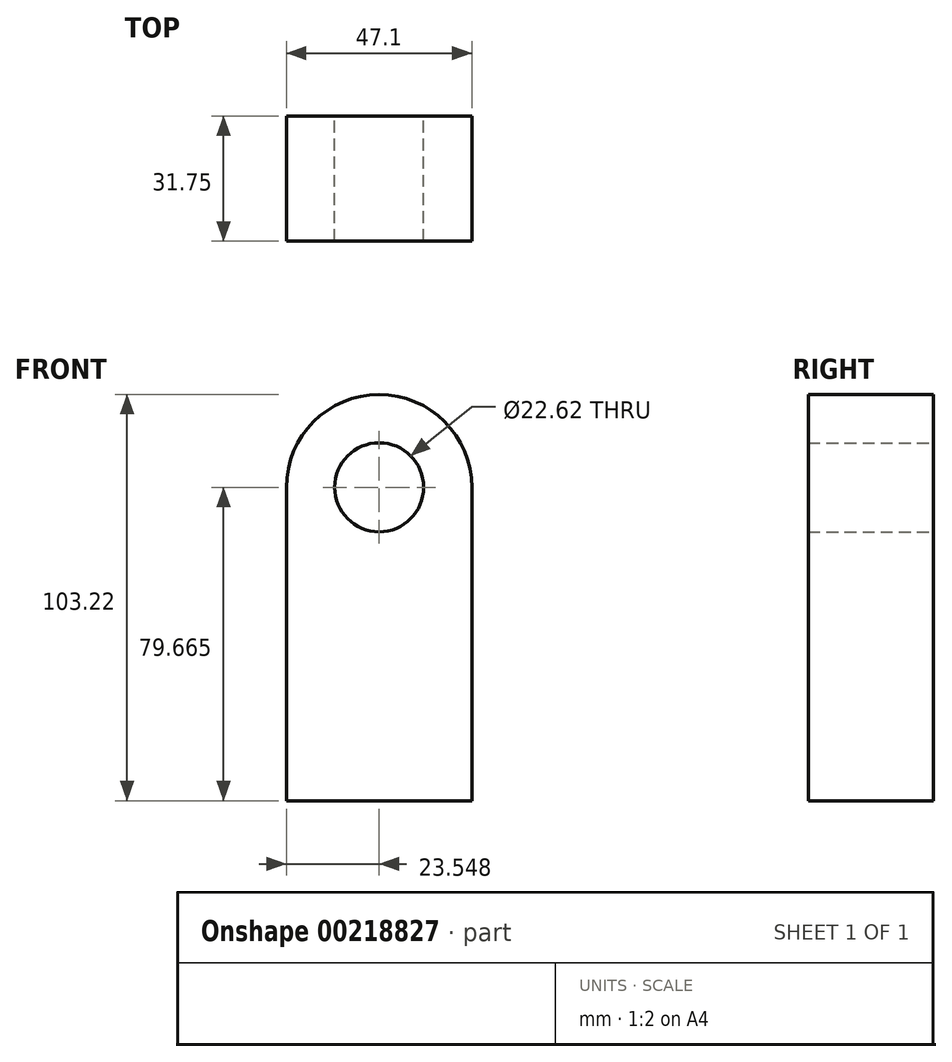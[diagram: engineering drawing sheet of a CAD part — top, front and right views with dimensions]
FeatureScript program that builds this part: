
annotation { "Feature Type Name" : "Feature", "Feature Type Description" : "" }
export const myFeature = defineFeature(function(context is Context, id is Id, definition is map)
    precondition{}
    {
        {
            var Q0;
            Q0=qCreatedBy(makeId("Front.planeOp"),FACE);
            var sketch = newSketch(context, id + "F0", { "sketchPlane" : qUnion([Q0])});
            skLineSegment(sketch, "E0.top", {"start": v(-21.47, -26.44) * mm, "end": v(25.63, -26.44) * mm});
            skLineSegment(sketch, "E0.left", {"start": v(-21.47, 53.22) * mm, "end": v(-21.47, -26.44) * mm});
            skLineSegment(sketch, "E0.right", {"start": v(25.63, 53.22) * mm, "end": v(25.63, -26.44) * mm});
            skArc(sketch, "E1", {"start": v(25.63, 53.22) * mm, "mid": v(2.08, 76.78) * mm, "end": v(-21.47, 53.22) * mm});
            skCircle(sketch, "E2", {"center": v(2.08, 53.22) * mm, "radius": 11.3 * mm});
            skSolve(sketch);
        }
        {
            var Q0;
            Q0=makeQuery(id+"F0.imprint","IMPRINT",FACE,{"disambiguationData":[TD([[makeQuery(id+"F0.imprint","IMPRINT",EDGE,{"derivedFrom":sQuery(id+"F0.wireOp",EDGE,"E0.top")}),1.0]])]});
            extrude(context, id + "F1", {"entities" : qUnion([Q0]), "depth" : 31.75 * mm});
        }
    });
